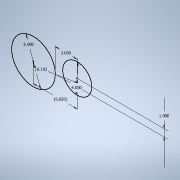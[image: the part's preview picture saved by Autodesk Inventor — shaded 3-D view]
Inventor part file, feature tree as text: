
AUTODESK INVENTOR PART (.ipt)
format: ipt  version: 2020 (Build 240168000, 168)  size: 91,136 bytes
history: native  units: in
note: dims shown in document units (in); Inventor stores cm internally (conversion verified against a paired STEP export)
features: sketch x1
ambient origin geometry x8: Origin, YZ Plane, XZ Plane, XY Plane, X Axis, Y Axis, Z Axis, Center Point
feature tree (1):
  sketch  "Sketch1"  dims[d0=6.0in d1=3.0in d2=4.0in d3=1.0in d5=6.1023in d6=6.0198in]
